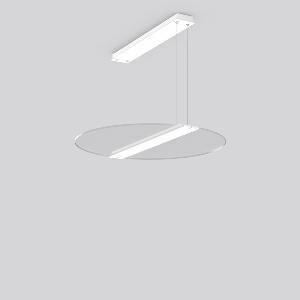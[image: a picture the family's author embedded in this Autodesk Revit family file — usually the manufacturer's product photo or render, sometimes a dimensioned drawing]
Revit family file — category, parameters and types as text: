
# Revit family: twindot_s_round_312353_002_76_5895
name_source: partatom
category: Lighting Fixtures
units: mm (PartAtom-declared; Revit-internal decimal feet)

## family parameters
Cut with Voids When Loaded = No
Host = Face
Light Source = No
Part Type = Normal
Room Calculation Point = No
Round Connector Dimension = Use Diameter
Shared = No

## types (1)
- TWINDOT S round (1 x LED Modul 830, 4500 lm, 3000)
    Apparent Load = 41 VA
    CIE Flux Codes = 49 78 94 56 100
    Color Rendering = 80
    Color Temperature = 3000
    Default Elevation = 1800 mm
    Description = Series: TWINDOT S round
LED pendant luminaire with extremely flat and frameless appearance. Middle bar made of aluminium extrusion profile, powder-coated. Transparent light guide made of UV-resistant acrylic glass (PMMA) with TWINDOT prismatic. Light control with perfectly glare-free TWINDOT technology for pleasantly gentle light with soft shadows. Even and wide indirect and direct light distribution. Direct 55%, indirect 45% light emission. 4-point steel cable suspension, steplessly adjustable. Converter integrated in the canopy (powder-coated white). Power supply through suspension cable. 
Colour: traffic white, matt (RAL 9016)
Diameter: 645 mm
Height: 20 mm
Suspension length: 500-1200 mm
Lamp: LED
Socket: without socket
Colour temperature: 3000K
Colour rendering index (CRI): 80
System power: 41 W
Rated luminous flux: 4500 lm
Luminous efficiency: 110 lm/W
Control gear: Converter, dimmable, DALI
Protection class: I
Type of protection: IP 20
    Height = 20 mm  [stored 0.0656168 ft]
    Lamp = 1 x LED Modul 830
    Lamp Light Flux = 4500 lm
    Lamp count = 1
    Length = 645 mm
    Lifetime = 50000 h
    Luminous efficacy = 110 lm/W
    Manufacturer = RZB
    ModVariant = No
    Model = 312353.002.76
    Mounting Place = Ceiling
    Mounting Type = Pendant
    Number of Poles = 1
    OnlyDefault = Yes
    Power Factor = 1
    Product Name = TWINDOT S round
    Product group = Pendant modular luminaires
    ProductGroupID = 906
    Protection Class = Protection class I
    Protection Degree = IP 20
    RLX_Detail_Level = 1
    RLX_Emergency_Light_Flux = 0 lm
    RLX_Emergency_Type = 0
    RLX_Emergency_Type_DB = No
    RlxData = <blob elided: 36077 chars, md5=17140155>
    Socket = socket
    Standby Power = 0 W
    System Light Flux = 4500 lm
    System Power = 41 W
    Type Comments = Product without accessories
    Type Image = 312353.002.jpg
    URL = http://relux.com
    VarID = ---
    Voltage = 230 V
    Voltage Range = 220-240 V
    Weight = 0.00 kg
    Width = 0 mm  [stored 0 ft]

note: [stored X ft] marks values corroborated as IEEE doubles in the binary element streams (Revit-internal decimal feet)

## geometry (parser evidence)
native form markers: Blend x4, Sweep x11
no freeform markers — native parametric forms only
